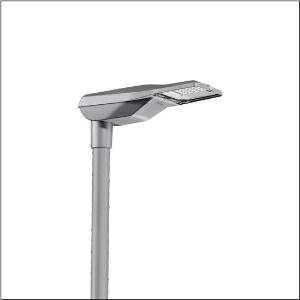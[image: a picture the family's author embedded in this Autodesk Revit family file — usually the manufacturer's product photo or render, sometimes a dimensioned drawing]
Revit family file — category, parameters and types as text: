
# Revit family: streetlight_sl_21_iq_micro___stw1_0a_5xe1e31g08cb_d673
name_source: partatom
category: Lighting Fixtures
units: mm (PartAtom-declared; Revit-internal decimal feet)

## family parameters
Cut with Voids When Loaded = No
Host = Face
Light Source = No
Part Type = Normal
Room Calculation Point = No
Round Connector Dimension = Use Diameter
Shared = No

## types (1)
- --- (1 x LED, 2870 lm, 19.4 W, 3000K)
    Apparent Load = 19 VA
    CIE Flux Codes = 38 75 98 100 100
    Color Rendering = 70
    Color Temperature = 3000K
    Default Elevation = 1800 mm
    Description = Streetlight SL 21 iQ micro, mast luminaire, primary light control with lens, of PMMA, primary optical cover: cover, of toughened safety glass, transparent, light distribution: STW1.0a, light emission: direct distribution, primary light characteristic: asymmetric, installation type: post-top, side-entry, LED, High Power LED, rated luminous flux: 2.870lm, luminous efficacy: 148lm/W, light colour: 730, colour temperature: 3000K, control: Street-Remote, Auto-Match, Temp-Guard, Lumen-Switch, Night-Set, Smart-Wire, Light-Fading, Desk-Remote (wireless, voltage-free reading and setting of iQ features in the workshop via application-optimized NFC function/RFID function), optimised constant luminous flux control (CLO 2.0), pre-setting: linear dimming characteristic, mains connection: 220..240V, AC, 50/60Hz, start of lifetime: 19W, end of service life: 20W, reduction: 10W, luminaire housing, of diecast aluminium, powder-coated, Siteco® metallic grey (DB 702S), corrosivity category C5 mid according to DIN EN ISO 12944, please order mast flange separately, inclination adjustable: 0°, 5°, 10°, 15°, sealing non-destructively replaceable, multi-level sealing system, length: 528mm, width: 235mm, height: 110mm, mast flange for spigot size: 42mm (side-entry): 5XC10008XM4, 60/48mm (side-entry/post-top): 5XC10108XM2, 76/60mm (side-entry/post-top): 5XC10108XM1, protection rating (complete): IP66, insulation class (complete): insulation class II (safety insulation), certification: CE, ENEC, ENEC+, VDE, impact resistance: IK09, permissible operating ambient temperature for outdoor applications: -40..+50°C, standard-compliant lighting for roads and squares, packaging unit: 1 piece

Light Distribution: STW1.0a
    Height = 110 mm
    Lamp = 1 x LED
    Lamp Light Flux = 2870 lm
    Lamp Power = 19.4 W
    Lamp count = 1
    Length = 528 mm
    Luminous efficacy = 148 lm/W
    Manufacturer = Siteco
    ModVariant = No
    Model = 5XE1E31G08CB
    Number of Poles = 1
    OnlyDefault = Yes
    Power Factor = 1
    Product Name = Streetlight SL 21 iQ micro | STW1.0a
    Product group = mast luminaire | pylon top
    ProductGroupID = 6100
    Protection Class = Protection class II
    Protection Degree = IP 66
    RLX_Detail_Level = 1
    RLX_Emergency_Light_Flux = 0 lm
    RLX_Emergency_Type = 0
    RLX_Emergency_Type_DB = No
    RlxData = <blob elided: 98737 chars, md5=e5b6d5bf>
    Socket = socket
    Standby Power = 0 W
    System Light Flux = 2870 lm
    System Power = 19 W
    Type Comments = factory setting: luminous flux: 100 % | dim-lin: 254 | 387 mA
    Type Image = l_1006881.jpg
    URL = http://relux.com
    VarID = @adj_108663
    Voltage = 0 V
    Weight = 0.00 kg
    Width = 235 mm

## geometry (parser evidence)
native form markers: Blend x4, Sweep x12
no freeform markers — native parametric forms only
